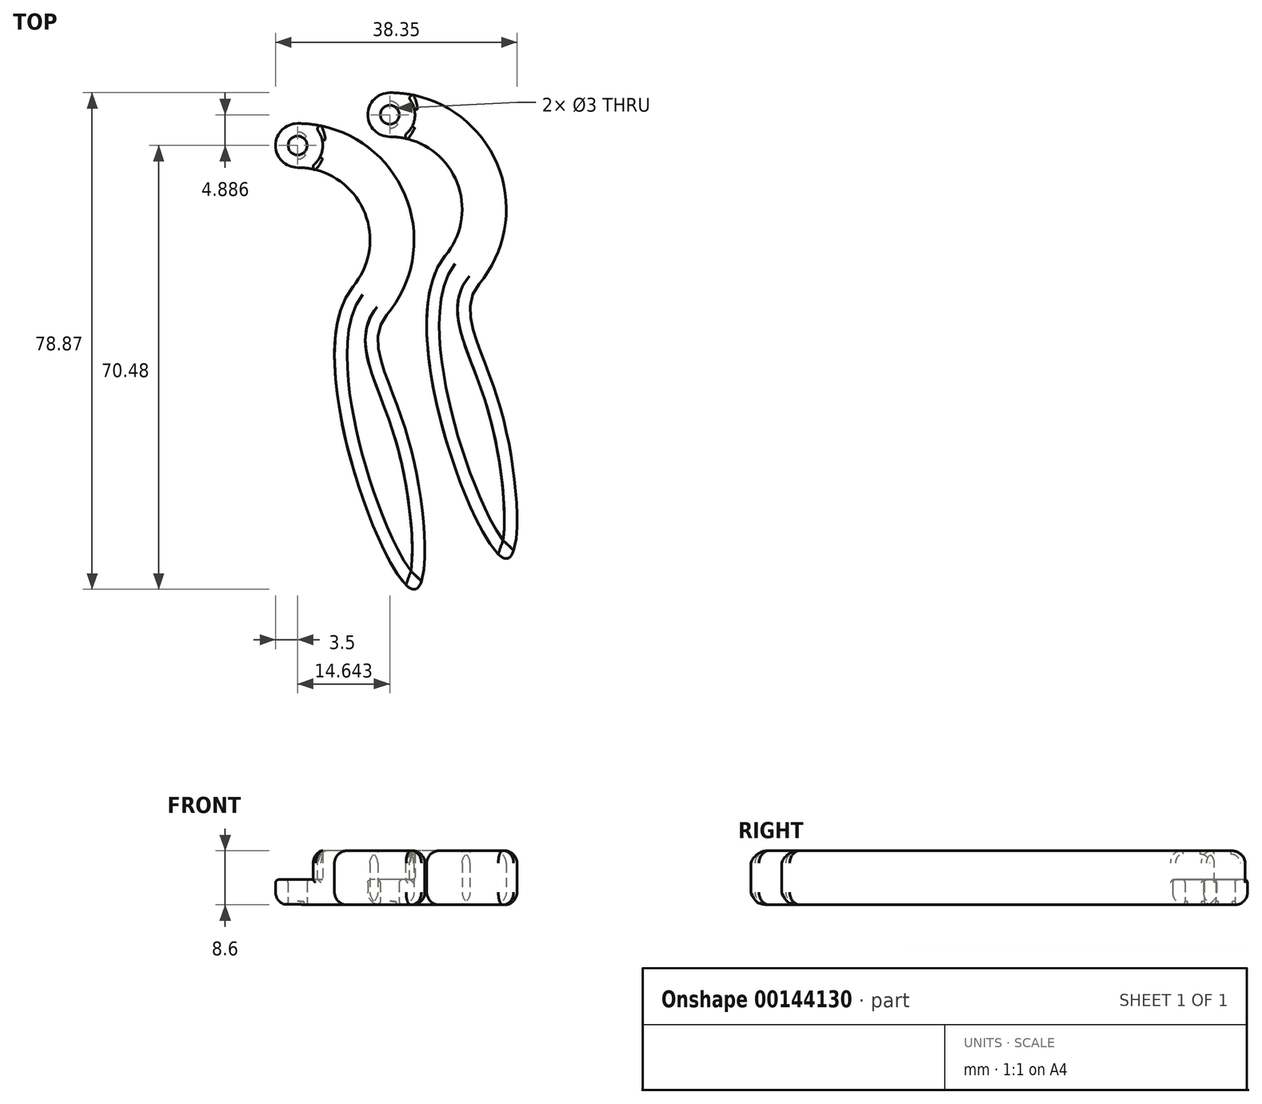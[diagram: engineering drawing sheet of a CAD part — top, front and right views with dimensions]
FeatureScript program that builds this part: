
annotation { "Feature Type Name" : "Feature", "Feature Type Description" : "" }
export const myFeature = defineFeature(function(context is Context, id is Id, definition is map)
    precondition{}
    {
        {
            var Q0;
            Q0=qCreatedBy(makeId("Top.planeOp"),FACE);
            var sketch = newSketch(context, id + "F0", { "sketchPlane" : qUnion([Q0])});
            skArc(sketch, "E0", {"start": v(8.8, -7.4) * mm, "mid": v(10.42, 4.86) * mm, "end": v(0, 11.5) * mm});
            skCircle(sketch, "E1", {"center": v(0, 15) * mm, "radius": 1.5 * mm});
            skArc(sketch, "E2", {"start": v(14.17, -11.9) * mm, "mid": v(16.77, 7.82) * mm, "end": v(0, 18.5) * mm});
            skArc(sketch, "E3", {"start": v(0, 18.5) * mm, "mid": v(-3.5, 15) * mm, "end": v(0, 11.5) * mm});
            skLineSegment(sketch, "E4", {"start": v(0, 0) * mm, "end": v(14.17, -11.9) * mm, "construction": true});
            skFitSpline(sketch, "E5", {"points": [v(8.8, -7.4) * mm, v(18.06, -55.38) * mm, v(17.65, -31.85) * mm, v(14.17, -11.9) * mm], "startDerivative": vector(-61.78, -73.63) * mm, "endDerivative": vector(40.94, 48.8) * mm});
            skArc(sketch, "E6", {"start": v(1.7, 11.38) * mm, "mid": v(4, 14.74) * mm, "end": v(2.15, 18.38) * mm});
            skLineSegment(sketch, "E7", {"start": v(0, 0) * mm, "end": v(14.64, 4.89) * mm, "construction": true});
            skSolve(sketch);
        }
        {
            var Q0;
            {var subQ0=sQuery(id+"F0.wireOp",EDGE,"E5");Q0=makeQuery(id+"F0.imprint","IMPRINT",FACE,{"disambiguationData":[TD([[makeQuery(id+"F0.imprint","IMPRINT",EDGE,{"derivedFrom":subQ0}),1.0]])]});}
            extrude(context, id + "F1", {"entities" : qUnion([Q0]), "depth" : 8.6 * mm});
        }
        {
            var Q0;
            Q0=makeQuery(id+"F0.imprint","IMPRINT",FACE,{"disambiguationData":[TD([[makeQuery(id+"F0.imprint","IMPRINT",EDGE,{"derivedFrom":sQuery(id+"F0.wireOp",EDGE,"E1")}),-1.0]])]});
            extrude(context, id + "F2", {"entities" : qUnion([Q0]), "operationType" : NewBodyOperationType.ADD, "depth" : 4 * mm});
        }
        {
            var Q0;
            Q0=makeQuery(id+"F1.opExtrude","CAP_EDGE",EDGE,{"disambiguationData":[OSD([sQuery(id+"F0.wireOp",EDGE,"E5")])],"isStart":false});
            var Q1;
            {var subQ0=sQuery(id+"F0.wireOp",EDGE,"E2");Q1=makeQuery(id+"F2.boolean.opBoolean","MERGE",EDGE,{"derivedFrom":[makeQuery(id+"F1.opExtrude","CAP_EDGE",EDGE,{"disambiguationData":[OSD([subQ0])],"isStart":true}),makeQuery(id+"F2.opExtrude","CAP_EDGE",EDGE,{"disambiguationData":[OSD([subQ0])],"isStart":true})]});}
            fillet(context, id + "F3", {"entities" : qUnion([Q0, Q1]), "radius" : 2 * mm, "tangentPropagation" : true, "allowEdgeOverflow" : false});
        }
        {
            var Q0;
            Q0=makeQuery(id+"F2.opExtrude","CAP_EDGE",EDGE,{"disambiguationData":[OSD([sQuery(id+"F0.wireOp",EDGE,"E3")])],"isStart":false});
            var Q1;
            Q1=makeQuery(id+"F1.opExtrude","SWEPT_EDGE",EDGE,{"disambiguationData":[OSD([sQuery(id+"F0.wireOp",EDGE,"E2"),sQuery(id+"F0.wireOp",EDGE,"E6")])]});
            var Q2;
            Q2=makeQuery(id+"F2.opExtrude","CAP_EDGE",EDGE,{"disambiguationData":[OSD([sQuery(id+"F0.wireOp",EDGE,"E1")])],"isStart":false});
            var Q3;
            Q3=makeQuery(id+"F2.opExtrude","CAP_EDGE",EDGE,{"disambiguationData":[OSD([sQuery(id+"F0.wireOp",EDGE,"E1")])],"isStart":true});
            fillet(context, id + "F4", {"entities" : qUnion([Q0, Q1, Q2, Q3]), "radius" : 0.5 * mm, "tangentPropagation" : true, "allowEdgeOverflow" : false});
        }
        {
            var Q0;
            Q0=makeQuery(id+"F1.opExtrude","SWEPT_BODY",BODY,{"disambiguationData":[OSD([sQuery(id+"F0.wireOp",EDGE,"E0"),sQuery(id+"F0.wireOp",EDGE,"E2"),sQuery(id+"F0.wireOp",EDGE,"E5"),sQuery(id+"F0.wireOp",EDGE,"E6")])]});
            var Q1;
            Q1=sQuery(id+"F0.wireOp",EDGE,"E7");
            transform(context, id + "F5", {"entities" : qUnion([Q0]), "transformType" : TransformType.TRANSLATION_ENTITY, "oppositeDirectionEntity" : false, "transformLine" : qUnion([Q1]), "makeCopy" : true});
        }
    });
